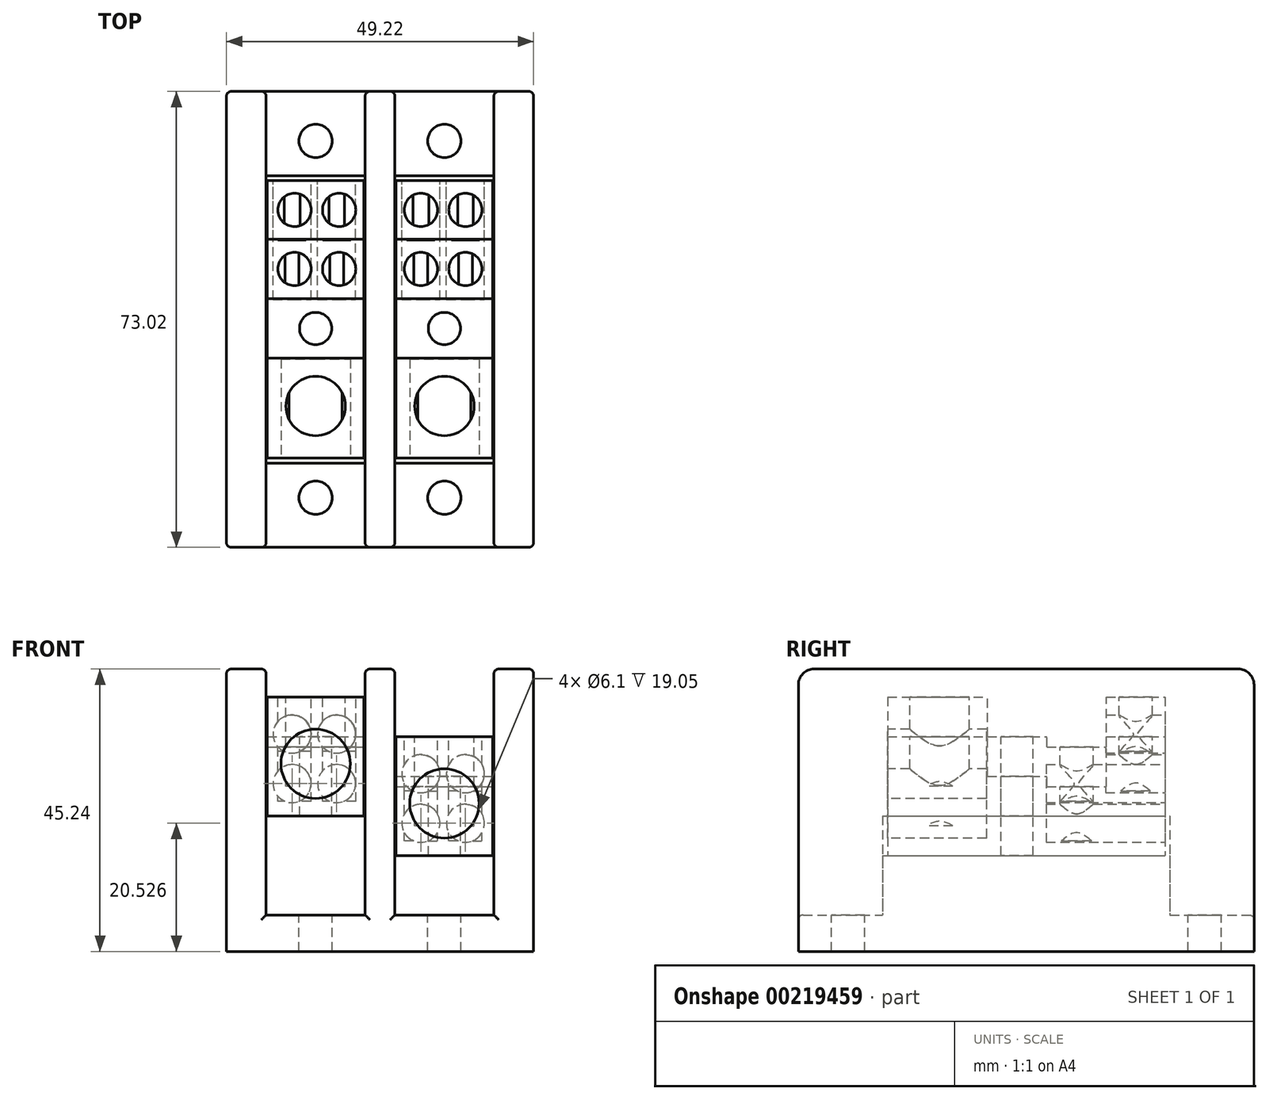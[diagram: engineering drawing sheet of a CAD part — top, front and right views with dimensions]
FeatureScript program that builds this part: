
annotation { "Feature Type Name" : "Feature", "Feature Type Description" : "" }
export const myFeature = defineFeature(function(context is Context, id is Id, definition is map)
    precondition{}
    {
        {
            var Q0;
            Q0=qCreatedBy(makeId("Top.planeOp"),FACE);
            var sketch = newSketch(context, id + "F0", { "sketchPlane" : qUnion([Q0])});
            skLineSegment(sketch, "E0.bottom", {"start": v(-24.6, -36.51) * mm, "end": v(24.6, -36.51) * mm});
            skLineSegment(sketch, "E0.top", {"start": v(-24.6, 36.51) * mm, "end": v(24.6, 36.51) * mm});
            skLineSegment(sketch, "E0.left", {"start": v(-24.6, -36.51) * mm, "end": v(-24.6, 36.51) * mm});
            skLineSegment(sketch, "E0.right", {"start": v(24.6, -36.51) * mm, "end": v(24.6, 36.51) * mm});
            skPoint(sketch, "E0.middle", {"position": v(0, 0) * mm});
            skSolve(sketch);
        }
        {
            var Q0;
            Q0=qSketchRegion(id+"F0",true);
            extrude(context, id + "F1", {"entities" : qUnion([Q0]), "depth" : 45.24 * mm});
        }
        {
            var Q0;
            Q0=makeQuery(id+"F1.opExtrude","CAP_FACE",FACE,{"disambiguationData":[OSD([sQuery(id+"F0.wireOp",EDGE,"E0.bottom"),sQuery(id+"F0.wireOp",EDGE,"E0.top"),sQuery(id+"F0.wireOp",EDGE,"E0.left"),sQuery(id+"F0.wireOp",EDGE,"E0.right")])],"isStart":false});
            var sketch = newSketch(context, id + "F2", { "sketchPlane" : qUnion([Q0])});
            skLineSegment(sketch, "E1.bottom", {"start": v(-2.38, -36.51) * mm, "end": v(-18.26, -36.51) * mm});
            skLineSegment(sketch, "E1.top", {"start": v(-2.38, 36.51) * mm, "end": v(-18.26, 36.51) * mm});
            skLineSegment(sketch, "E1.left", {"start": v(-2.38, -36.51) * mm, "end": v(-2.38, 36.51) * mm});
            skLineSegment(sketch, "E1.right", {"start": v(-18.26, -36.51) * mm, "end": v(-18.26, 36.51) * mm});
            skPoint(sketch, "E1.middle", {"position": v(-10.32, 0) * mm});
            skPoint(sketch, "E2.middle", {"position": v(0, 0) * mm});
            skLineSegment(sketch, "E3.bottom", {"start": v(18.26, -36.51) * mm, "end": v(2.38, -36.51) * mm});
            skLineSegment(sketch, "E3.top", {"start": v(18.26, 36.51) * mm, "end": v(2.38, 36.51) * mm});
            skLineSegment(sketch, "E3.left", {"start": v(18.26, -36.51) * mm, "end": v(18.26, 36.51) * mm});
            skLineSegment(sketch, "E3.right", {"start": v(2.38, -36.51) * mm, "end": v(2.38, 36.51) * mm});
            skPoint(sketch, "E3.middle", {"position": v(10.32, 0) * mm});
            skSolve(sketch);
        }
        {
            var Q0;
            Q0=qSketchRegion(id+"F2",true);
            extrude(context, id + "F3", {"entities" : qUnion([Q0]), "operationType" : NewBodyOperationType.REMOVE, "oppositeDirection" : true, "depth" : 39.4 * mm});
        }
        {
            var Q0;
            Q0=makeQuery(id+"F3.boolean.opBoolean","COPY",FACE,{"derivedFrom":makeQuery(id+"F3.opExtrude","CAP_FACE",FACE,{"disambiguationData":[OSD([sQuery(id+"F2.wireOp",EDGE,"E1.bottom"),sQuery(id+"F2.wireOp",EDGE,"E1.top"),sQuery(id+"F2.wireOp",EDGE,"E1.left"),sQuery(id+"F2.wireOp",EDGE,"E1.right")])],"isStart":false})});
            var sketch = newSketch(context, id + "F4", { "sketchPlane" : qUnion([Q0])});
            skCircle(sketch, "E4", {"center": v(-10.32, 28.58) * mm, "radius": 2.67 * mm});
            skCircle(sketch, "E5", {"center": v(-10.32, -28.58) * mm, "radius": 2.67 * mm});
            skCircle(sketch, "E6", {"center": v(10.32, 28.58) * mm, "radius": 2.67 * mm});
            skCircle(sketch, "E7", {"center": v(10.32, -28.58) * mm, "radius": 2.67 * mm});
            skSolve(sketch);
        }
        {
            var Q0;
            Q0=qSketchRegion(id+"F4",true);
            extrude(context, id + "F5", {"entities" : qUnion([Q0]), "operationType" : NewBodyOperationType.REMOVE, "oppositeDirection" : true, "depth" : 5.84 * mm});
        }
        {
            var Q0;
            {var subQ0=sQuery(id+"F0.wireOp",EDGE,"E0.left");var subQ1=sQuery(id+"F0.wireOp",EDGE,"E0.top");Q0=makeQuery(id+"F3.boolean.opBoolean","SPLIT",EDGE,{"disambiguationData":[TD([makeQuery(id+"F1.opExtrude","SWEPT_FACE",FACE,{"disambiguationData":[OSD([subQ0])]})])],"derivedFrom":makeQuery(id+"F1.opExtrude","CAP_EDGE",EDGE,{"disambiguationData":[OSD([subQ1])],"isStart":false})});}
            var Q1;
            {var subQ0=sQuery(id+"F0.wireOp",EDGE,"E0.top");Q1=makeQuery(id+"F3.boolean.opBoolean","SPLIT",EDGE,{"disambiguationData":[TD([makeQuery(id+"F3.opExtrude","SWEPT_FACE",FACE,{"disambiguationData":[OSD([sQuery(id+"F2.wireOp",EDGE,"E1.left")])]})])],"derivedFrom":makeQuery(id+"F1.opExtrude","CAP_EDGE",EDGE,{"disambiguationData":[OSD([subQ0])],"isStart":false})});}
            var Q2;
            {var subQ0=sQuery(id+"F0.wireOp",EDGE,"E0.right");var subQ1=sQuery(id+"F0.wireOp",EDGE,"E0.top");Q2=makeQuery(id+"F3.boolean.opBoolean","SPLIT",EDGE,{"disambiguationData":[TD([makeQuery(id+"F1.opExtrude","SWEPT_FACE",FACE,{"disambiguationData":[OSD([subQ0])]})])],"derivedFrom":makeQuery(id+"F1.opExtrude","CAP_EDGE",EDGE,{"disambiguationData":[OSD([subQ1])],"isStart":false})});}
            var Q3;
            {var subQ0=sQuery(id+"F0.wireOp",EDGE,"E0.bottom");var subQ1=sQuery(id+"F0.wireOp",EDGE,"E0.left");Q3=makeQuery(id+"F3.boolean.opBoolean","SPLIT",EDGE,{"disambiguationData":[TD([makeQuery(id+"F1.opExtrude","SWEPT_FACE",FACE,{"disambiguationData":[OSD([subQ1])]})])],"derivedFrom":makeQuery(id+"F1.opExtrude","CAP_EDGE",EDGE,{"disambiguationData":[OSD([subQ0])],"isStart":false})});}
            var Q4;
            {var subQ0=sQuery(id+"F0.wireOp",EDGE,"E0.bottom");Q4=makeQuery(id+"F3.boolean.opBoolean","SPLIT",EDGE,{"disambiguationData":[TD([makeQuery(id+"F3.opExtrude","SWEPT_FACE",FACE,{"disambiguationData":[OSD([sQuery(id+"F2.wireOp",EDGE,"E1.left")])]})])],"derivedFrom":makeQuery(id+"F1.opExtrude","CAP_EDGE",EDGE,{"disambiguationData":[OSD([subQ0])],"isStart":false})});}
            var Q5;
            {var subQ0=sQuery(id+"F0.wireOp",EDGE,"E0.bottom");var subQ1=sQuery(id+"F0.wireOp",EDGE,"E0.right");Q5=makeQuery(id+"F3.boolean.opBoolean","SPLIT",EDGE,{"disambiguationData":[TD([makeQuery(id+"F1.opExtrude","SWEPT_FACE",FACE,{"disambiguationData":[OSD([subQ1])]})])],"derivedFrom":makeQuery(id+"F1.opExtrude","CAP_EDGE",EDGE,{"disambiguationData":[OSD([subQ0])],"isStart":false})});}
            fillet(context, id + "F6", {"entities" : qUnion([Q0, Q1, Q2, Q3, Q4, Q5]), "radius" : 2.54 * mm, "tangentPropagation" : true});
        }
        {
            var Q0;
            Q0=makeQuery(id+"F3.boolean.opBoolean","COPY",EDGE,{"derivedFrom":makeQuery(id+"F3.opExtrude","CAP_EDGE",EDGE,{"disambiguationData":[OSD([sQuery(id+"F2.wireOp",EDGE,"E1.top")])],"isStart":false})});
            var Q1;
            Q1=makeQuery(id+"F3.boolean.opBoolean","COPY",EDGE,{"derivedFrom":makeQuery(id+"F3.opExtrude","CAP_EDGE",EDGE,{"disambiguationData":[OSD([sQuery(id+"F2.wireOp",EDGE,"E3.top")])],"isStart":false})});
            var Q2;
            Q2=makeQuery(id+"F3.boolean.opBoolean","COPY",EDGE,{"derivedFrom":makeQuery(id+"F3.opExtrude","CAP_EDGE",EDGE,{"disambiguationData":[OSD([sQuery(id+"F2.wireOp",EDGE,"E1.bottom")])],"isStart":false})});
            var Q3;
            Q3=makeQuery(id+"F3.boolean.opBoolean","COPY",EDGE,{"derivedFrom":makeQuery(id+"F3.opExtrude","CAP_EDGE",EDGE,{"disambiguationData":[OSD([sQuery(id+"F2.wireOp",EDGE,"E3.bottom")])],"isStart":false})});
            var Q4;
            Q4=makeQuery(id+"F1.opExtrude","SWEPT_EDGE",EDGE,{"disambiguationData":[OSD([sQuery(id+"F0.wireOp",EDGE,"E0.bottom"),sQuery(id+"F0.wireOp",EDGE,"E0.left")])]});
            var Q5;
            Q5=makeQuery(id+"F3.boolean.opBoolean","COPY",EDGE,{"derivedFrom":makeQuery(id+"F3.opExtrude","SWEPT_EDGE",EDGE,{"disambiguationData":[OSD([sQuery(id+"F0.wireOp",EDGE,"E0.bottom"),sQuery(id+"F2.wireOp",EDGE,"E1.bottom"),sQuery(id+"F2.wireOp",EDGE,"E1.right")])]})});
            var Q6;
            Q6=makeQuery(id+"F3.boolean.opBoolean","COPY",EDGE,{"derivedFrom":makeQuery(id+"F3.opExtrude","SWEPT_EDGE",EDGE,{"disambiguationData":[OSD([sQuery(id+"F0.wireOp",EDGE,"E0.bottom"),sQuery(id+"F2.wireOp",EDGE,"E3.bottom"),sQuery(id+"F2.wireOp",EDGE,"E3.right")])]})});
            var Q7;
            Q7=makeQuery(id+"F1.opExtrude","SWEPT_EDGE",EDGE,{"disambiguationData":[OSD([sQuery(id+"F0.wireOp",EDGE,"E0.bottom"),sQuery(id+"F0.wireOp",EDGE,"E0.right")])]});
            var Q8;
            Q8=makeQuery(id+"F3.boolean.opBoolean","COPY",EDGE,{"derivedFrom":makeQuery(id+"F3.opExtrude","SWEPT_EDGE",EDGE,{"disambiguationData":[OSD([sQuery(id+"F0.wireOp",EDGE,"E0.bottom"),sQuery(id+"F2.wireOp",EDGE,"E3.bottom"),sQuery(id+"F2.wireOp",EDGE,"E3.left")])]})});
            var Q9;
            Q9=makeQuery(id+"F3.boolean.opBoolean","COPY",EDGE,{"derivedFrom":makeQuery(id+"F3.opExtrude","SWEPT_EDGE",EDGE,{"disambiguationData":[OSD([sQuery(id+"F0.wireOp",EDGE,"E0.bottom"),sQuery(id+"F2.wireOp",EDGE,"E1.bottom"),sQuery(id+"F2.wireOp",EDGE,"E1.left")])]})});
            fillet(context, id + "F7", {"entities" : qUnion([Q0, Q1, Q2, Q3, Q4, Q5, Q6, Q7, Q8, Q9]), "radius" : 0.76 * mm, "tangentPropagation" : true});
        }
        {
            var Q0;
            Q0=makeQuery(id+"F3.boolean.opBoolean","COPY",FACE,{"derivedFrom":makeQuery(id+"F3.opExtrude","CAP_FACE",FACE,{"disambiguationData":[OSD([sQuery(id+"F2.wireOp",EDGE,"E1.bottom"),sQuery(id+"F2.wireOp",EDGE,"E1.top"),sQuery(id+"F2.wireOp",EDGE,"E1.left"),sQuery(id+"F2.wireOp",EDGE,"E1.right")])],"isStart":false})});
            var sketch = newSketch(context, id + "F8", { "sketchPlane" : qUnion([Q0])});
            skLineSegment(sketch, "E8.bottom", {"start": v(-18.26, 23.02) * mm, "end": v(-2.38, 23.02) * mm});
            skLineSegment(sketch, "E8.top", {"start": v(-18.26, -23.02) * mm, "end": v(-2.38, -23.02) * mm});
            skLineSegment(sketch, "E8.left", {"start": v(-18.26, 23.02) * mm, "end": v(-18.26, -23.02) * mm});
            skLineSegment(sketch, "E8.right", {"start": v(-2.38, 23.02) * mm, "end": v(-2.38, -23.02) * mm});
            skSolve(sketch);
        }
        {
            var Q0;
            Q0=qSketchRegion(id+"F8",true);
            extrude(context, id + "F9", {"entities" : qUnion([Q0]), "operationType" : NewBodyOperationType.ADD, "depth" : 15.88 * mm});
        }
        {
            var Q0;
            Q0=makeQuery(id+"F3.boolean.opBoolean","COPY",FACE,{"derivedFrom":makeQuery(id+"F3.opExtrude","CAP_FACE",FACE,{"disambiguationData":[OSD([sQuery(id+"F2.wireOp",EDGE,"E3.bottom"),sQuery(id+"F2.wireOp",EDGE,"E3.top"),sQuery(id+"F2.wireOp",EDGE,"E3.left"),sQuery(id+"F2.wireOp",EDGE,"E3.right")])],"isStart":false})});
            var sketch = newSketch(context, id + "F10", { "sketchPlane" : qUnion([Q0])});
            skLineSegment(sketch, "E9.bottom", {"start": v(2.38, 23.02) * mm, "end": v(18.26, 23.02) * mm});
            skLineSegment(sketch, "E9.top", {"start": v(2.38, -23.02) * mm, "end": v(18.26, -23.02) * mm});
            skLineSegment(sketch, "E9.left", {"start": v(2.38, 23.02) * mm, "end": v(2.38, -23.02) * mm});
            skLineSegment(sketch, "E9.right", {"start": v(18.26, 23.02) * mm, "end": v(18.26, -23.02) * mm});
            skSolve(sketch);
        }
        {
            var Q0;
            Q0=qSketchRegion(id+"F10",true);
            extrude(context, id + "F11", {"entities" : qUnion([Q0]), "operationType" : NewBodyOperationType.ADD, "depth" : 9.52 * mm});
        }
        {
            var Q0;
            Q0=makeQuery(id+"F9.opExtrude","CAP_FACE",FACE,{"disambiguationData":[OSD([sQuery(id+"F8.wireOp",EDGE,"E8.bottom"),sQuery(id+"F8.wireOp",EDGE,"E8.top"),sQuery(id+"F8.wireOp",EDGE,"E8.left"),sQuery(id+"F8.wireOp",EDGE,"E8.right")])],"isStart":false});
            var sketch = newSketch(context, id + "F12", { "sketchPlane" : qUnion([Q0])});
            skLineSegment(sketch, "E10.bottom", {"start": v(-18.06, -22.23) * mm, "end": v(-2.58, -22.23) * mm});
            skLineSegment(sketch, "E10.top", {"start": v(-18.06, 22.23) * mm, "end": v(-2.58, 22.23) * mm});
            skLineSegment(sketch, "E10.left", {"start": v(-18.06, -22.23) * mm, "end": v(-18.06, 22.23) * mm});
            skLineSegment(sketch, "E10.right", {"start": v(-2.58, -22.23) * mm, "end": v(-2.58, 22.23) * mm});
            skPoint(sketch, "E10.middle", {"position": v(-10.32, 0) * mm});
            skSolve(sketch);
        }
        {
            var Q0;
            Q0=makeQuery(id+"F12.imprint","IMPRINT",FACE,{"disambiguationData":[TD([[makeQuery(id+"F12.imprint","IMPRINT",EDGE,{"derivedFrom":sQuery(id+"F12.wireOp",EDGE,"E10.bottom")}),1.0]])]});
            extrude(context, id + "F13", {"entities" : qUnion([Q0]), "depth" : 19.05 * mm});
        }
        {
            var Q0;
            Q0=makeQuery(id+"F11.opExtrude","CAP_FACE",FACE,{"disambiguationData":[OSD([sQuery(id+"F10.wireOp",EDGE,"E9.bottom"),sQuery(id+"F10.wireOp",EDGE,"E9.top"),sQuery(id+"F10.wireOp",EDGE,"E9.left"),sQuery(id+"F10.wireOp",EDGE,"E9.right")])],"isStart":false});
            var sketch = newSketch(context, id + "F14", { "sketchPlane" : qUnion([Q0])});
            skLineSegment(sketch, "E11.bottom", {"start": v(2.58, -22.22) * mm, "end": v(18.06, -22.22) * mm});
            skLineSegment(sketch, "E11.top", {"start": v(2.58, 22.23) * mm, "end": v(18.06, 22.23) * mm});
            skLineSegment(sketch, "E11.left", {"start": v(2.58, -22.23) * mm, "end": v(2.58, 22.23) * mm});
            skLineSegment(sketch, "E11.right", {"start": v(18.06, -22.23) * mm, "end": v(18.06, 22.23) * mm});
            skPoint(sketch, "E11.middle", {"position": v(10.32, 0) * mm});
            skSolve(sketch);
        }
        {
            var Q0;
            Q0=qSketchRegion(id+"F14",true);
            extrude(context, id + "F15", {"entities" : qUnion([Q0]), "depth" : 19.05 * mm});
        }
        {
            var Q0;
            Q0=makeQuery(id+"F13.opExtrude","CAP_FACE",FACE,{"disambiguationData":[OSD([sQuery(id+"F12.wireOp",EDGE,"E10.bottom"),sQuery(id+"F12.wireOp",EDGE,"E10.top"),sQuery(id+"F12.wireOp",EDGE,"E10.left"),sQuery(id+"F12.wireOp",EDGE,"E10.right")])],"isStart":false});
            var sketch = newSketch(context, id + "F16", { "sketchPlane" : qUnion([Q0])});
            skCircle(sketch, "E12", {"center": v(-10.32, -13.9) * mm, "radius": 4.76 * mm});
            skSolve(sketch);
        }
        {
            var Q0;
            Q0=qSketchRegion(id+"F16",true);
            extrude(context, id + "F17", {"entities" : qUnion([Q0]), "operationType" : NewBodyOperationType.REMOVE, "oppositeDirection" : true, "depth" : 14.29 * mm});
        }
        {
            var Q0;
            Q0=makeQuery(id+"F15.opExtrude","CAP_FACE",FACE,{"disambiguationData":[OSD([sQuery(id+"F14.wireOp",EDGE,"E11.bottom"),sQuery(id+"F14.wireOp",EDGE,"E11.top"),sQuery(id+"F14.wireOp",EDGE,"E11.left"),sQuery(id+"F14.wireOp",EDGE,"E11.right")])],"isStart":false});
            var sketch = newSketch(context, id + "F18", { "sketchPlane" : qUnion([Q0])});
            skPoint(sketch, "E13.centerSnap0", {"position": v(10.32, 22.23) * mm});
            skCircle(sketch, "E14", {"center": v(10.32, -13.9) * mm, "radius": 4.76 * mm});
            skSolve(sketch);
        }
        {
            var Q0;
            Q0=qSketchRegion(id+"F18",true);
            extrude(context, id + "F19", {"entities" : qUnion([Q0]), "operationType" : NewBodyOperationType.REMOVE, "oppositeDirection" : true, "depth" : 14.29 * mm});
        }
        {
            var Q0;
            Q0=makeQuery(id+"F13.opExtrude","SWEPT_FACE",FACE,{"disambiguationData":[OSD([sQuery(id+"F12.wireOp",EDGE,"E10.bottom")])]});
            var sketch = newSketch(context, id + "F20", { "sketchPlane" : qUnion([Q0])});
            skCircle(sketch, "E15", {"center": v(-10.32, 30.05) * mm, "radius": 5.56 * mm});
            skPoint(sketch, "E15.centerSnap0", {"position": v(-10.32, 40.77) * mm});
            skSolve(sketch);
        }
        {
            var Q0;
            Q0=qSketchRegion(id+"F20",true);
            extrude(context, id + "F21", {"entities" : qUnion([Q0]), "operationType" : NewBodyOperationType.REMOVE, "oppositeDirection" : true, "depth" : 15.88 * mm});
        }
        {
            var Q0;
            Q0=makeQuery(id+"F15.opExtrude","SWEPT_FACE",FACE,{"disambiguationData":[OSD([sQuery(id+"F14.wireOp",EDGE,"E11.bottom")])]});
            var sketch = newSketch(context, id + "F22", { "sketchPlane" : qUnion([Q0])});
            skCircle(sketch, "E16", {"center": v(10.32, 23.7) * mm, "radius": 5.56 * mm});
            skPoint(sketch, "E16.centerSnap0", {"position": v(10.32, 34.42) * mm});
            skSolve(sketch);
        }
        {
            var Q0;
            Q0=qSketchRegion(id+"F22",true);
            extrude(context, id + "F23", {"entities" : qUnion([Q0]), "operationType" : NewBodyOperationType.REMOVE, "oppositeDirection" : true, "depth" : 15.88 * mm});
        }
        {
            var Q0;
            Q0=makeQuery(id+"F13.opExtrude","CAP_FACE",FACE,{"disambiguationData":[OSD([sQuery(id+"F12.wireOp",EDGE,"E10.bottom"),sQuery(id+"F12.wireOp",EDGE,"E10.top"),sQuery(id+"F12.wireOp",EDGE,"E10.left"),sQuery(id+"F12.wireOp",EDGE,"E10.right")])],"isStart":false});
            var sketch = newSketch(context, id + "F24", { "sketchPlane" : qUnion([Q0])});
            skLineSegment(sketch, "E17.bottom", {"start": v(-18.06, -6.22) * mm, "end": v(-2.58, -6.22) * mm});
            skLineSegment(sketch, "E17.top", {"start": v(-18.06, 3.3) * mm, "end": v(-2.58, 3.3) * mm});
            skLineSegment(sketch, "E17.left", {"start": v(-18.06, -6.22) * mm, "end": v(-18.06, 3.3) * mm});
            skLineSegment(sketch, "E17.right", {"start": v(-2.58, -6.22) * mm, "end": v(-2.58, 3.3) * mm});
            skSolve(sketch);
        }
        {
            var Q0;
            Q0=makeQuery(id+"F15.opExtrude","CAP_FACE",FACE,{"disambiguationData":[OSD([sQuery(id+"F14.wireOp",EDGE,"E11.bottom"),sQuery(id+"F14.wireOp",EDGE,"E11.top"),sQuery(id+"F14.wireOp",EDGE,"E11.left"),sQuery(id+"F14.wireOp",EDGE,"E11.right")])],"isStart":false});
            var sketch = newSketch(context, id + "F25", { "sketchPlane" : qUnion([Q0])});
            skLineSegment(sketch, "E18.bottom", {"start": v(2.58, -6.22) * mm, "end": v(18.06, -6.22) * mm});
            skLineSegment(sketch, "E18.top", {"start": v(2.58, 3.3) * mm, "end": v(18.06, 3.3) * mm});
            skLineSegment(sketch, "E18.left", {"start": v(2.58, -6.22) * mm, "end": v(2.58, 3.3) * mm});
            skLineSegment(sketch, "E18.right", {"start": v(18.06, -6.22) * mm, "end": v(18.06, 3.3) * mm});
            skSolve(sketch);
        }
        {
            var Q0;
            Q0=qSketchRegion(id+"F24",true);
            extrude(context, id + "F26", {"entities" : qUnion([Q0]), "operationType" : NewBodyOperationType.REMOVE, "oppositeDirection" : true, "depth" : 6.35 * mm});
        }
        {
            var Q0;
            Q0=qSketchRegion(id+"F25",true);
            extrude(context, id + "F27", {"entities" : qUnion([Q0]), "operationType" : NewBodyOperationType.REMOVE, "oppositeDirection" : true, "depth" : 6.35 * mm});
        }
        {
            var Q0;
            {var subQ0=sQuery(id+"F12.wireOp",EDGE,"E10.top");var subQ1=sQuery(id+"F12.wireOp",EDGE,"E10.left");var subQ2=sQuery(id+"F12.wireOp",EDGE,"E10.right");Q0=makeQuery(id+"F26.boolean.opBoolean","SPLIT",FACE,{"disambiguationData":[TD([makeQuery(id+"F13.opExtrude","SWEPT_FACE",FACE,{"disambiguationData":[OSD([subQ0])]})])],"derivedFrom":makeQuery(id+"F13.opExtrude","CAP_FACE",FACE,{"disambiguationData":[OSD([sQuery(id+"F12.wireOp",EDGE,"E10.bottom"),subQ0,subQ1,subQ2])],"isStart":false})});}
            var sketch = newSketch(context, id + "F28", { "sketchPlane" : qUnion([Q0])});
            skLineSegment(sketch, "E19.bottom", {"start": v(-18.06, 3.3) * mm, "end": v(-2.58, 3.3) * mm});
            skLineSegment(sketch, "E19.top", {"start": v(-18.06, 12.83) * mm, "end": v(-2.58, 12.83) * mm});
            skLineSegment(sketch, "E19.left", {"start": v(-18.06, 3.3) * mm, "end": v(-18.06, 12.83) * mm});
            skLineSegment(sketch, "E19.right", {"start": v(-2.58, 3.3) * mm, "end": v(-2.58, 12.83) * mm});
            skSolve(sketch);
        }
        {
            var Q0;
            Q0=qSketchRegion(id+"F28",true);
            extrude(context, id + "F29", {"entities" : qUnion([Q0]), "operationType" : NewBodyOperationType.REMOVE, "oppositeDirection" : true, "depth" : 8 * mm});
        }
        {
            var Q0;
            {var subQ0=sQuery(id+"F14.wireOp",EDGE,"E11.top");var subQ1=sQuery(id+"F14.wireOp",EDGE,"E11.left");var subQ2=sQuery(id+"F14.wireOp",EDGE,"E11.right");Q0=makeQuery(id+"F27.boolean.opBoolean","SPLIT",FACE,{"disambiguationData":[TD([makeQuery(id+"F15.opExtrude","SWEPT_FACE",FACE,{"disambiguationData":[OSD([subQ0])]})])],"derivedFrom":makeQuery(id+"F15.opExtrude","CAP_FACE",FACE,{"disambiguationData":[OSD([sQuery(id+"F14.wireOp",EDGE,"E11.bottom"),subQ0,subQ1,subQ2])],"isStart":false})});}
            var sketch = newSketch(context, id + "F30", { "sketchPlane" : qUnion([Q0])});
            skLineSegment(sketch, "E20.bottom", {"start": v(2.58, 3.3) * mm, "end": v(18.06, 3.3) * mm});
            skLineSegment(sketch, "E20.top", {"start": v(2.58, 12.83) * mm, "end": v(18.06, 12.83) * mm});
            skLineSegment(sketch, "E20.left", {"start": v(2.58, 3.3) * mm, "end": v(2.58, 12.83) * mm});
            skLineSegment(sketch, "E20.right", {"start": v(18.06, 3.3) * mm, "end": v(18.06, 12.83) * mm});
            skSolve(sketch);
        }
        {
            var Q0;
            Q0=makeQuery(id+"F30.imprint","IMPRINT",FACE,{"disambiguationData":[TD([[makeQuery(id+"F30.imprint","IMPRINT",EDGE,{"derivedFrom":sQuery(id+"F30.wireOp",EDGE,"E20.bottom")}),1.0]])]});
            extrude(context, id + "F31", {"entities" : qUnion([Q0]), "operationType" : NewBodyOperationType.REMOVE, "oppositeDirection" : true, "depth" : 8 * mm});
        }
        {
            var Q0;
            Q0=makeQuery(id+"F15.opExtrude","SWEPT_FACE",FACE,{"disambiguationData":[OSD([sQuery(id+"F14.wireOp",EDGE,"E11.top")])]});
            var sketch = newSketch(context, id + "F32", { "sketchPlane" : qUnion([Q0])});
            skCircle(sketch, "E21", {"center": v(-13.7, 28.46) * mm, "radius": 3.05 * mm});
            skCircle(sketch, "E22", {"center": v(-6.55, 28.46) * mm, "radius": 3.05 * mm});
            skSolve(sketch);
        }
        {
            var Q0;
            Q0=qSketchRegion(id+"F32",true);
            extrude(context, id + "F33", {"entities" : qUnion([Q0]), "operationType" : NewBodyOperationType.REMOVE, "oppositeDirection" : true, "depth" : 9.52 * mm});
        }
        {
            var Q0;
            Q0=makeQuery(id+"F15.opExtrude","SWEPT_FACE",FACE,{"disambiguationData":[OSD([sQuery(id+"F14.wireOp",EDGE,"E11.top")])]});
            var sketch = newSketch(context, id + "F34", { "sketchPlane" : qUnion([Q0])});
            skCircle(sketch, "E23", {"center": v(-13.7, 20.53) * mm, "radius": 3.05 * mm});
            skCircle(sketch, "E24", {"center": v(-6.55, 20.53) * mm, "radius": 3.05 * mm});
            skSolve(sketch);
        }
        {
            var Q0;
            Q0=qSketchRegion(id+"F34",true);
            extrude(context, id + "F35", {"entities" : qUnion([Q0]), "operationType" : NewBodyOperationType.REMOVE, "oppositeDirection" : true, "depth" : 19.05 * mm});
        }
        {
            var Q0;
            {var subQ0=sQuery(id+"F14.wireOp",EDGE,"E11.top");var subQ1=sQuery(id+"F14.wireOp",EDGE,"E11.left");var subQ2=sQuery(id+"F14.wireOp",EDGE,"E11.right");Q0=makeQuery(id+"F27.boolean.opBoolean","SPLIT",FACE,{"disambiguationData":[TD([makeQuery(id+"F15.opExtrude","SWEPT_FACE",FACE,{"disambiguationData":[OSD([subQ0])]})])],"derivedFrom":makeQuery(id+"F15.opExtrude","CAP_FACE",FACE,{"disambiguationData":[OSD([sQuery(id+"F14.wireOp",EDGE,"E11.bottom"),subQ0,subQ1,subQ2])],"isStart":false})});}
            var sketch = newSketch(context, id + "F36", { "sketchPlane" : qUnion([Q0])});
            skCircle(sketch, "E25", {"center": v(6.55, 17.53) * mm, "radius": 2.67 * mm});
            skCircle(sketch, "E26", {"center": v(13.7, 17.53) * mm, "radius": 2.67 * mm});
            skSolve(sketch);
        }
        {
            var Q0;
            Q0=qSketchRegion(id+"F36",true);
            extrude(context, id + "F37", {"entities" : qUnion([Q0]), "operationType" : NewBodyOperationType.REMOVE, "oppositeDirection" : true, "depth" : 8.73 * mm});
        }
        {
            var Q0;
            Q0=makeQuery(id+"F31.boolean.opBoolean","COPY",FACE,{"derivedFrom":makeQuery(id+"F31.opExtrude","CAP_FACE",FACE,{"disambiguationData":[OSD([sQuery(id+"F30.wireOp",EDGE,"E20.bottom"),sQuery(id+"F30.wireOp",EDGE,"E20.top"),sQuery(id+"F30.wireOp",EDGE,"E20.left"),sQuery(id+"F30.wireOp",EDGE,"E20.right")])],"isStart":false})});
            var sketch = newSketch(context, id + "F38", { "sketchPlane" : qUnion([Q0])});
            skCircle(sketch, "E27", {"center": v(6.55, 8.06) * mm, "radius": 2.67 * mm});
            skCircle(sketch, "E28", {"center": v(13.7, 8.06) * mm, "radius": 2.67 * mm});
            skSolve(sketch);
        }
        {
            var Q0;
            Q0=qSketchRegion(id+"F38",true);
            extrude(context, id + "F39", {"entities" : qUnion([Q0]), "operationType" : NewBodyOperationType.REMOVE, "oppositeDirection" : true, "depth" : 8.73 * mm});
        }
        {
            var Q0;
            Q0=makeQuery(id+"F27.boolean.opBoolean","COPY",FACE,{"derivedFrom":makeQuery(id+"F27.opExtrude","CAP_FACE",FACE,{"disambiguationData":[OSD([sQuery(id+"F25.wireOp",EDGE,"E18.bottom"),sQuery(id+"F25.wireOp",EDGE,"E18.top"),sQuery(id+"F25.wireOp",EDGE,"E18.left"),sQuery(id+"F25.wireOp",EDGE,"E18.right")])],"isStart":false})});
            var sketch = newSketch(context, id + "F40", { "sketchPlane" : qUnion([Q0])});
            skCircle(sketch, "E29", {"center": v(10.32, -1.46) * mm, "radius": 2.58 * mm});
            skSolve(sketch);
        }
        {
            var Q0;
            Q0=qSketchRegion(id+"F40",true);
            extrude(context, id + "F41", {"entities" : qUnion([Q0]), "operationType" : NewBodyOperationType.REMOVE, "oppositeDirection" : true, "depth" : 12.7 * mm});
        }
        {
            var Q0;
            Q0=makeQuery(id+"F26.boolean.opBoolean","COPY",FACE,{"derivedFrom":makeQuery(id+"F26.opExtrude","CAP_FACE",FACE,{"disambiguationData":[OSD([sQuery(id+"F24.wireOp",EDGE,"E17.bottom"),sQuery(id+"F24.wireOp",EDGE,"E17.top"),sQuery(id+"F24.wireOp",EDGE,"E17.left"),sQuery(id+"F24.wireOp",EDGE,"E17.right")])],"isStart":false})});
            var sketch = newSketch(context, id + "F42", { "sketchPlane" : qUnion([Q0])});
            skCircle(sketch, "E30", {"center": v(-10.32, -1.46) * mm, "radius": 2.58 * mm});
            skSolve(sketch);
        }
        {
            var Q0;
            Q0=qSketchRegion(id+"F42",true);
            extrude(context, id + "F43", {"entities" : qUnion([Q0]), "operationType" : NewBodyOperationType.REMOVE, "oppositeDirection" : true, "depth" : 12.7 * mm});
        }
        {
            var Q0;
            {var subQ0=sQuery(id+"F12.wireOp",EDGE,"E10.top");var subQ1=sQuery(id+"F12.wireOp",EDGE,"E10.left");var subQ2=sQuery(id+"F12.wireOp",EDGE,"E10.right");Q0=makeQuery(id+"F26.boolean.opBoolean","SPLIT",FACE,{"disambiguationData":[TD([makeQuery(id+"F13.opExtrude","SWEPT_FACE",FACE,{"disambiguationData":[OSD([subQ0])]})])],"derivedFrom":makeQuery(id+"F13.opExtrude","CAP_FACE",FACE,{"disambiguationData":[OSD([sQuery(id+"F12.wireOp",EDGE,"E10.bottom"),subQ0,subQ1,subQ2])],"isStart":false})});}
            var sketch = newSketch(context, id + "F44", { "sketchPlane" : qUnion([Q0])});
            skCircle(sketch, "E31", {"center": v(-13.7, 17.53) * mm, "radius": 2.67 * mm});
            skPoint(sketch, "E31.centerSnap0", {"position": v(-18.06, 17.53) * mm});
            skCircle(sketch, "E32", {"center": v(-6.55, 17.53) * mm, "radius": 2.67 * mm});
            skSolve(sketch);
        }
        {
            var Q0;
            Q0=qSketchRegion(id+"F44",true);
            extrude(context, id + "F45", {"entities" : qUnion([Q0]), "operationType" : NewBodyOperationType.REMOVE, "oppositeDirection" : true, "depth" : 8.73 * mm});
        }
        {
            var Q0;
            Q0=makeQuery(id+"F29.boolean.opBoolean","COPY",FACE,{"derivedFrom":makeQuery(id+"F29.opExtrude","CAP_FACE",FACE,{"disambiguationData":[OSD([sQuery(id+"F28.wireOp",EDGE,"E19.bottom"),sQuery(id+"F28.wireOp",EDGE,"E19.top"),sQuery(id+"F28.wireOp",EDGE,"E19.left"),sQuery(id+"F28.wireOp",EDGE,"E19.right")])],"isStart":false})});
            var sketch = newSketch(context, id + "F46", { "sketchPlane" : qUnion([Q0])});
            skCircle(sketch, "E33", {"center": v(-13.7, 8.06) * mm, "radius": 2.67 * mm});
            skPoint(sketch, "E33.centerSnap0", {"position": v(-18.06, 8.06) * mm});
            skCircle(sketch, "E34", {"center": v(-6.55, 8.06) * mm, "radius": 2.67 * mm});
            skSolve(sketch);
        }
        {
            var Q0;
            Q0=qSketchRegion(id+"F46",true);
            extrude(context, id + "F47", {"entities" : qUnion([Q0]), "operationType" : NewBodyOperationType.REMOVE, "oppositeDirection" : true, "depth" : 8.73 * mm});
        }
        {
            var Q0;
            Q0=makeQuery(id+"F13.opExtrude","SWEPT_FACE",FACE,{"disambiguationData":[OSD([sQuery(id+"F12.wireOp",EDGE,"E10.top")])]});
            var sketch = newSketch(context, id + "F48", { "sketchPlane" : qUnion([Q0])});
            skCircle(sketch, "E35", {"center": v(6.95, 34.81) * mm, "radius": 3.05 * mm});
            skCircle(sketch, "E36", {"center": v(14.09, 34.81) * mm, "radius": 3.05 * mm});
            skSolve(sketch);
        }
        {
            var Q0;
            Q0=qSketchRegion(id+"F48",true);
            extrude(context, id + "F49", {"entities" : qUnion([Q0]), "operationType" : NewBodyOperationType.REMOVE, "oppositeDirection" : true, "depth" : 9.52 * mm});
        }
        {
            var Q0;
            Q0=makeQuery(id+"F13.opExtrude","SWEPT_FACE",FACE,{"disambiguationData":[OSD([sQuery(id+"F12.wireOp",EDGE,"E10.top")])]});
            var sketch = newSketch(context, id + "F50", { "sketchPlane" : qUnion([Q0])});
            skCircle(sketch, "E37", {"center": v(6.95, 26.88) * mm, "radius": 3.05 * mm});
            skCircle(sketch, "E38", {"center": v(14.09, 26.88) * mm, "radius": 3.05 * mm});
            skSolve(sketch);
        }
        {
            var Q0;
            Q0=qSketchRegion(id+"F50",true);
            extrude(context, id + "F51", {"entities" : qUnion([Q0]), "operationType" : NewBodyOperationType.REMOVE, "oppositeDirection" : true, "depth" : 19.05 * mm});
        }
    });
